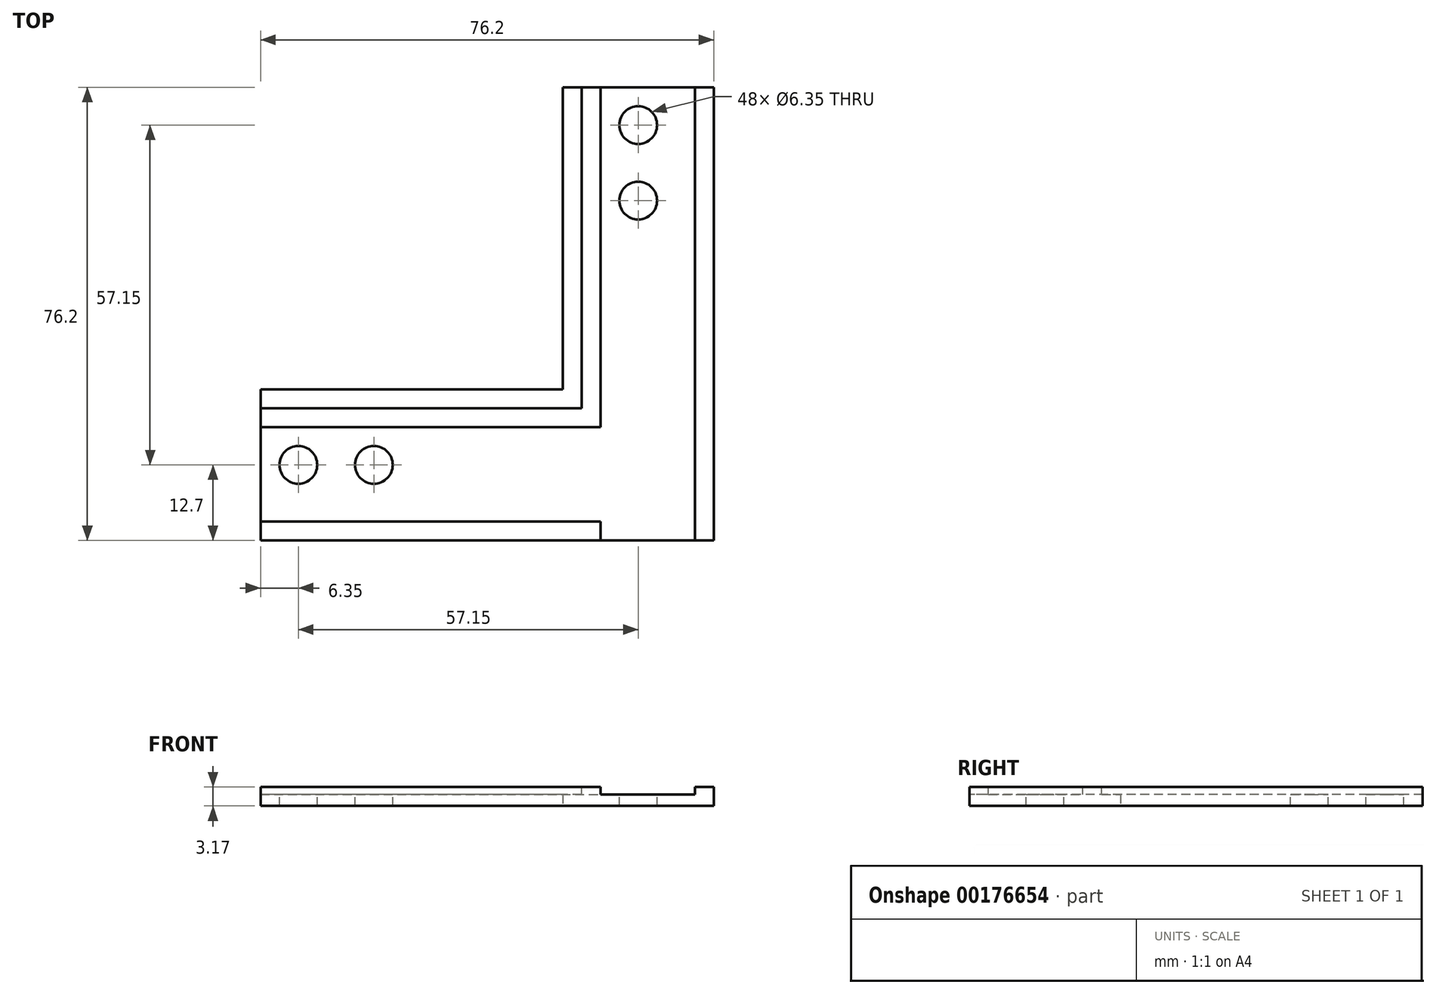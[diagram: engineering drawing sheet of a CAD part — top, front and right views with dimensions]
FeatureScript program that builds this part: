
annotation { "Feature Type Name" : "Feature", "Feature Type Description" : "" }
export const myFeature = defineFeature(function(context is Context, id is Id, definition is map)
    precondition{}
    {
        {
            var Q0;
            Q0=qCreatedBy(makeId("Top.planeOp"),FACE);
            var sketch = newSketch(context, id + "F0", { "sketchPlane" : qUnion([Q0])});
            skLineSegment(sketch, "E0.bottom", {"start": v(0, 0) * mm, "end": v(-76.2, 0) * mm});
            skLineSegment(sketch, "E0.top", {"start": v(0, 76.2) * mm, "end": v(-25.4, 76.2) * mm});
            skLineSegment(sketch, "E0.left", {"start": v(0, 0) * mm, "end": v(0, 76.2) * mm});
            skLineSegment(sketch, "E0.right", {"start": v(-76.2, 0) * mm, "end": v(-76.2, 25.4) * mm});
            skLineSegment(sketch, "E1.top", {"start": v(-25.4, 25.4) * mm, "end": v(-76.2, 25.4) * mm});
            skLineSegment(sketch, "E1.left", {"start": v(-25.4, 76.2) * mm, "end": v(-25.4, 25.4) * mm});
            skSolve(sketch);
        }
        {
            var Q0;
            Q0 = qSketchRegion(id + "F0", true);
            extrude(context, id + "F1", {"entities" : qUnion([Q0]), "depth" : 3.17 * mm});
        }
        {
            var Q0;
            Q0=makeQuery(id+"F1.opExtrude","CAP_FACE",FACE,{"disambiguationData":[OSD([sQuery(id+"F0.wireOp",EDGE,"E0.bottom"),sQuery(id+"F0.wireOp",EDGE,"E0.top"),sQuery(id+"F0.wireOp",EDGE,"E0.left"),sQuery(id+"F0.wireOp",EDGE,"E0.right"),sQuery(id+"F0.wireOp",EDGE,"E1.top"),sQuery(id+"F0.wireOp",EDGE,"E1.left")])],"isStart":false});
            var sketch = newSketch(context, id + "F2", { "sketchPlane" : qUnion([Q0])});
            skLineSegment(sketch, "E2.top", {"start": v(-25.4, 76.2) * mm, "end": v(-22.23, 76.2) * mm});
            skLineSegment(sketch, "E2.left", {"start": v(-25.4, 25.4) * mm, "end": v(-25.4, 76.2) * mm});
            skLineSegment(sketch, "E2.right", {"start": v(-22.23, 25.4) * mm, "end": v(-22.23, 76.2) * mm});
            skLineSegment(sketch, "E3.bottom", {"start": v(-25.4, 25.4) * mm, "end": v(-76.2, 25.4) * mm});
            skLineSegment(sketch, "E3.top", {"start": v(-25.4, 22.22) * mm, "end": v(-76.2, 22.22) * mm});
            skLineSegment(sketch, "E3.right", {"start": v(-76.2, 25.4) * mm, "end": v(-76.2, 22.22) * mm});
            skLineSegment(sketch, "E4.top", {"start": v(-22.23, 22.22) * mm, "end": v(-25.4, 22.22) * mm});
            skLineSegment(sketch, "E4.left", {"start": v(-22.23, 25.4) * mm, "end": v(-22.23, 22.22) * mm});
            skLineSegment(sketch, "E5.bottom", {"start": v(-19.05, 76.2) * mm, "end": v(-3.18, 76.2) * mm});
            skLineSegment(sketch, "E5.top", {"start": v(-19.05, 0) * mm, "end": v(-3.18, 0) * mm});
            skLineSegment(sketch, "E5.left", {"start": v(-19.05, 76.2) * mm, "end": v(-19.05, 19.05) * mm});
            skLineSegment(sketch, "E5.right", {"start": v(-3.18, 76.2) * mm, "end": v(-3.18, 0) * mm});
            skLineSegment(sketch, "E6.bottom", {"start": v(-76.2, 19.05) * mm, "end": v(-19.05, 19.05) * mm});
            skLineSegment(sketch, "E6.top", {"start": v(-76.2, 3.17) * mm, "end": v(-19.05, 3.17) * mm});
            skLineSegment(sketch, "E6.left", {"start": v(-76.2, 19.05) * mm, "end": v(-76.2, 3.17) * mm});
            skLineSegment(sketch, "E7.trimOffspring", {"start": v(-19.05, 3.17) * mm, "end": v(-19.05, 0) * mm});
            skSolve(sketch);
        }
        {
            var Q0;
            Q0 = qSketchRegion(id + "F2", true);
            extrude(context, id + "F3", {"entities" : qUnion([Q0]), "operationType" : NewBodyOperationType.REMOVE, "oppositeDirection" : true, "depth" : 1.27 * mm});
        }
        {
            var Q0;
            Q0=makeQuery(id+"F1.opExtrude","CAP_FACE",FACE,{"disambiguationData":[OSD([sQuery(id+"F0.wireOp",EDGE,"E0.bottom"),sQuery(id+"F0.wireOp",EDGE,"E0.top"),sQuery(id+"F0.wireOp",EDGE,"E0.left"),sQuery(id+"F0.wireOp",EDGE,"E0.right"),sQuery(id+"F0.wireOp",EDGE,"E1.top"),sQuery(id+"F0.wireOp",EDGE,"E1.left")])],"isStart":false});
            var sketch = newSketch(context, id + "F4", { "sketchPlane" : qUnion([Q0])});
            skCircle(sketch, "E8", {"center": v(-12.7, 69.85) * mm, "radius": 3.18 * mm});
            skCircle(sketch, "E9", {"center": v(-12.7, 57.15) * mm, "radius": 3.18 * mm});
            skCircle(sketch, "E10", {"center": v(-57.15, 12.7) * mm, "radius": 3.18 * mm});
            skCircle(sketch, "E11", {"center": v(-69.85, 12.7) * mm, "radius": 3.18 * mm});
            skSolve(sketch);
        }
        {
            var Q0;
            Q0 = qSketchRegion(id + "F4", true);
            extrude(context, id + "F5", {"entities" : qUnion([Q0]), "operationType" : NewBodyOperationType.REMOVE, "oppositeDirection" : true, "depth" : 25.4 * mm});
        }
    });
